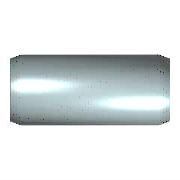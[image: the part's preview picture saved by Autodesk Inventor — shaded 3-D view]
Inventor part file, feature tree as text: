
AUTODESK INVENTOR PART (.ipt)
format: ipt  version: 2023.3 (Build 273359000, 359)  size: 115,200 bytes
history: native  units: mm (DEFAULTED — no unit token found)
features: extrude x1, chamfer x1, sketch x1
ambient origin geometry x8: Origin, YZ Plane, XZ Plane, XY Plane, X Axis, Y Axis, Z Axis, Center Point
bodies: Solid1 (feature_tree)
feature tree (3):
  extrude  "Körper"  Depth=12.0mm
  chamfer  "Skizze2"  [1 undecoded]
  sketch  "Skizze"  dims[d1=2.0mm d2=12.0mm d3=0.0mm d4=0.35mm d5=15.0deg d8=0.35mm d9=15.0deg d11=0.35mm d12=0.35mm d13=0.0mm d15=0.0mm d16=0.0mm]
note: 1 required parameter value undecoded (feature->parameter linkage not recoverable at this tier; creation-order binding heuristic only, values carry confidence <= 0.55)
